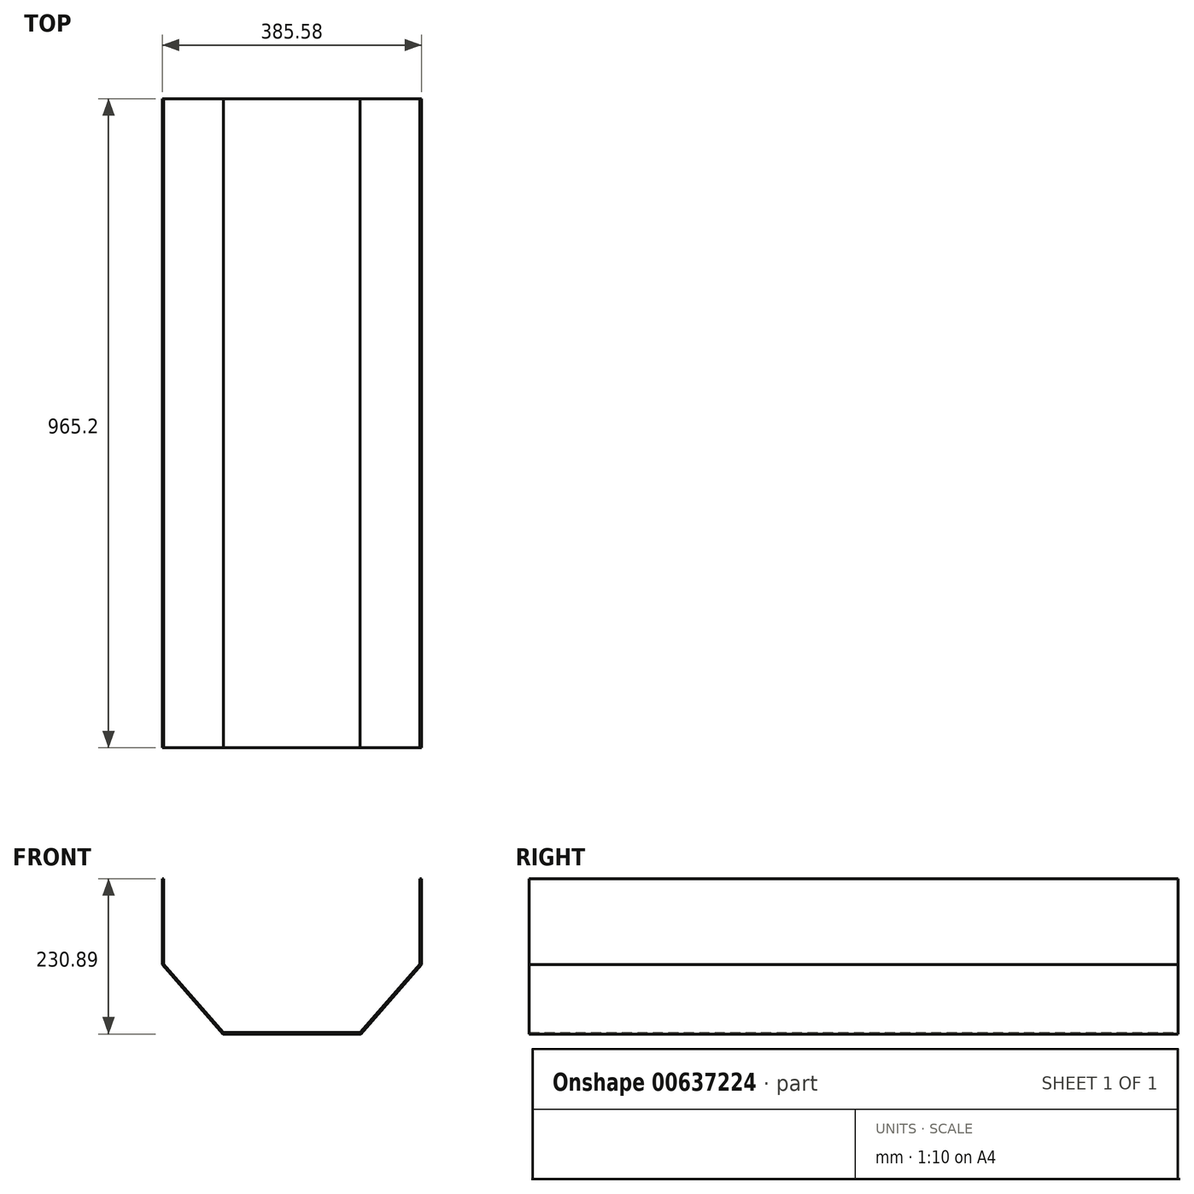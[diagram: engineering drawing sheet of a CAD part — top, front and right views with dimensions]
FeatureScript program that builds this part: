
annotation { "Feature Type Name" : "Feature", "Feature Type Description" : "" }
export const myFeature = defineFeature(function(context is Context, id is Id, definition is map)
    precondition{}
    {
        {
            var Q0;
            Q0=qCreatedBy(makeId("Front.planeOp"),FACE);
            var sketch = newSketch(context, id + "F0", { "sketchPlane" : qUnion([Q0])});
            skLineSegment(sketch, "E0", {"start": v(-88.9, 228.6) * mm, "end": v(-88.9, 101.6) * mm});
            skLineSegment(sketch, "E1", {"start": v(-88.9, 101.6) * mm, "end": v(0, 0) * mm});
            skLineSegment(sketch, "E2", {"start": v(0, 0) * mm, "end": v(203.2, 0) * mm});
            skLineSegment(sketch, "E3", {"start": v(203.2, 0) * mm, "end": v(292.1, 101.6) * mm});
            skLineSegment(sketch, "E4", {"start": v(292.1, 101.6) * mm, "end": v(292.1, 228.6) * mm});
            skLineSegment(sketch, "E5.0", {"start": v(294.39, 100.74) * mm, "end": v(294.39, 228.6) * mm});
            skLineSegment(sketch, "E5.1", {"start": v(-91.19, 228.6) * mm, "end": v(-91.19, 100.74) * mm});
            skLineSegment(sketch, "E5.2", {"start": v(-91.19, 100.74) * mm, "end": v(-1.04, -2.29) * mm});
            skLineSegment(sketch, "E5.3", {"start": v(-1.04, -2.29) * mm, "end": v(204.24, -2.29) * mm});
            skLineSegment(sketch, "E5.4", {"start": v(204.24, -2.29) * mm, "end": v(294.39, 100.74) * mm});
            skLineSegment(sketch, "E6", {"start": v(-91.19, 228.6) * mm, "end": v(-88.9, 228.6) * mm});
            skLineSegment(sketch, "E7", {"start": v(294.39, 228.6) * mm, "end": v(292.1, 228.6) * mm});
            skSolve(sketch);
        }
        {
            var Q0;
            Q0=makeQuery(id+"F0.imprint","IMPRINT",FACE,{"disambiguationData":[TD([[makeQuery(id+"F0.imprint","IMPRINT",EDGE,{"derivedFrom":sQuery(id+"F0.wireOp",EDGE,"jduJLrZv-X1GI-cXhU-0GYw-Lv6VTzxWPwgA")}),-1.0]])]});
            var Q1;
            Q1=makeQuery(id+"F0.imprint","IMPRINT",FACE,{"disambiguationData":[TD([[makeQuery(id+"F0.imprint","IMPRINT",EDGE,{"derivedFrom":sQuery(id+"F0.wireOp",EDGE,"E0")}),-1.0]])]});
            extrude(context, id + "F1", {"entities" : qUnion([Q0, Q1]), "depth" : 965.2 * mm, "offsetDistance" : 25.4 * mm});
        }
    });
